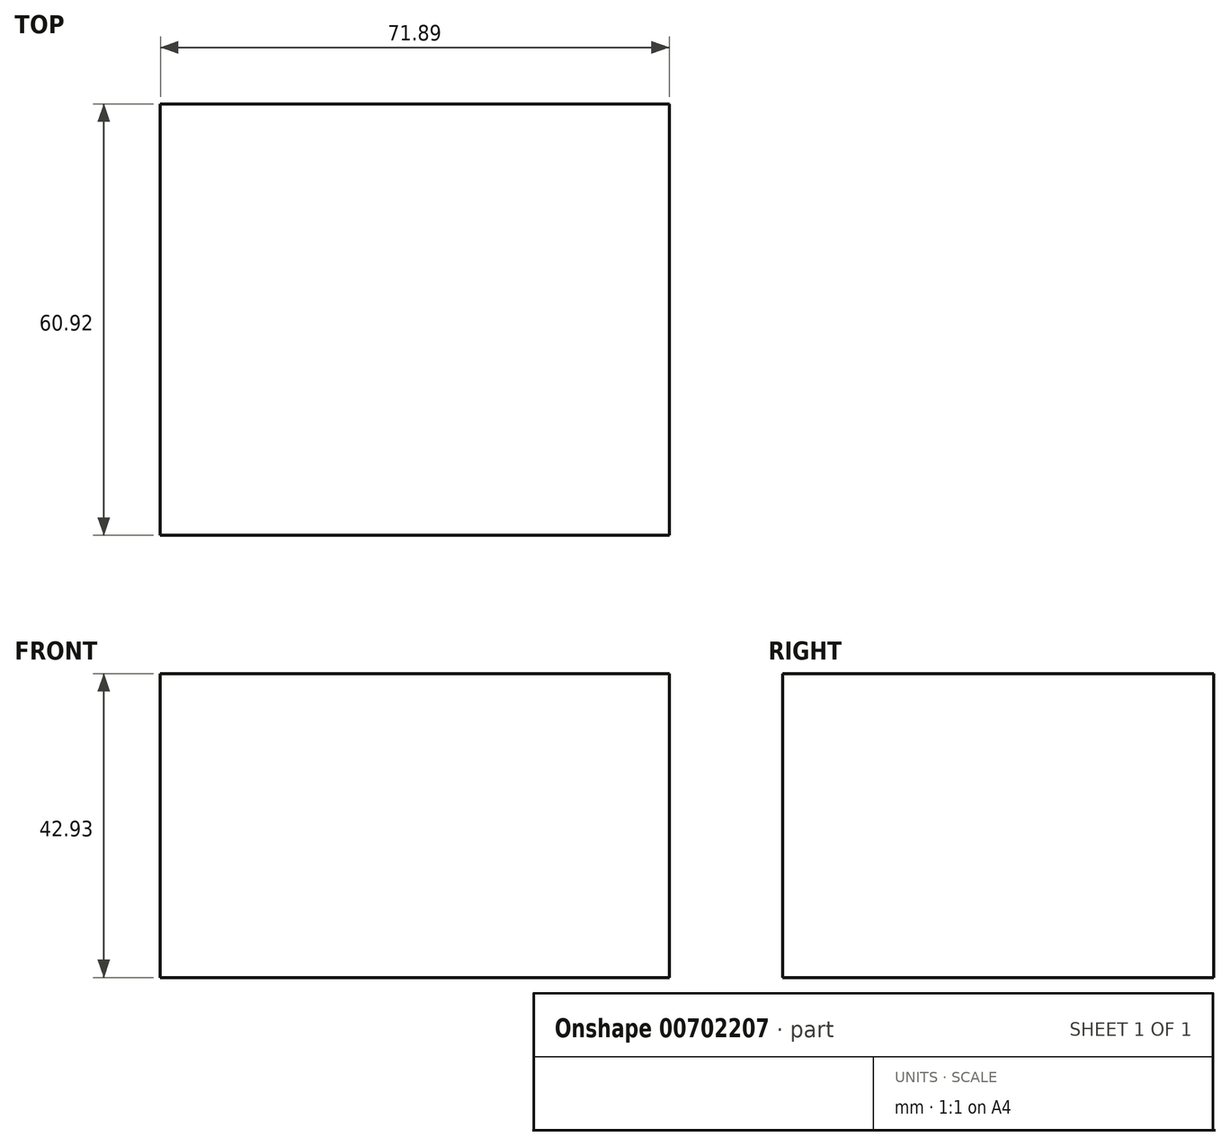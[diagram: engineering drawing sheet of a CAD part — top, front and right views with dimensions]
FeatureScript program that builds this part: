
annotation { "Feature Type Name" : "Feature", "Feature Type Description" : "" }
export const myFeature = defineFeature(function(context is Context, id is Id, definition is map)
    precondition{}
    {
        {
            var Q0;
            Q0=qCreatedBy(makeId("Top.planeOp"),FACE);
            var sketch = newSketch(context, id + "F0", { "sketchPlane" : qUnion([Q0])});
            skLineSegment(sketch, "E0.bottom", {"start": v(-44.56, 0) * mm, "end": v(27.33, 0) * mm});
            skLineSegment(sketch, "E0.top", {"start": v(-44.56, -60.92) * mm, "end": v(27.33, -60.92) * mm});
            skLineSegment(sketch, "E0.left", {"start": v(-44.56, 0) * mm, "end": v(-44.56, -60.92) * mm});
            skLineSegment(sketch, "E0.right", {"start": v(27.33, 0) * mm, "end": v(27.33, -60.92) * mm});
            skSolve(sketch);
        }
        {
            var Q0;
            Q0=makeQuery(id+"F0.imprint","IMPRINT",FACE,{"disambiguationData":[TD([[makeQuery(id+"F0.imprint","IMPRINT",EDGE,{"derivedFrom":sQuery(id+"F0.wireOp",EDGE,"E0.bottom")}),-1.0]])]});
            extrude(context, id + "F1", {"entities" : qUnion([Q0]), "depth" : 42.93 * mm, "offsetDistance" : 25.4 * mm});
        }
    });
